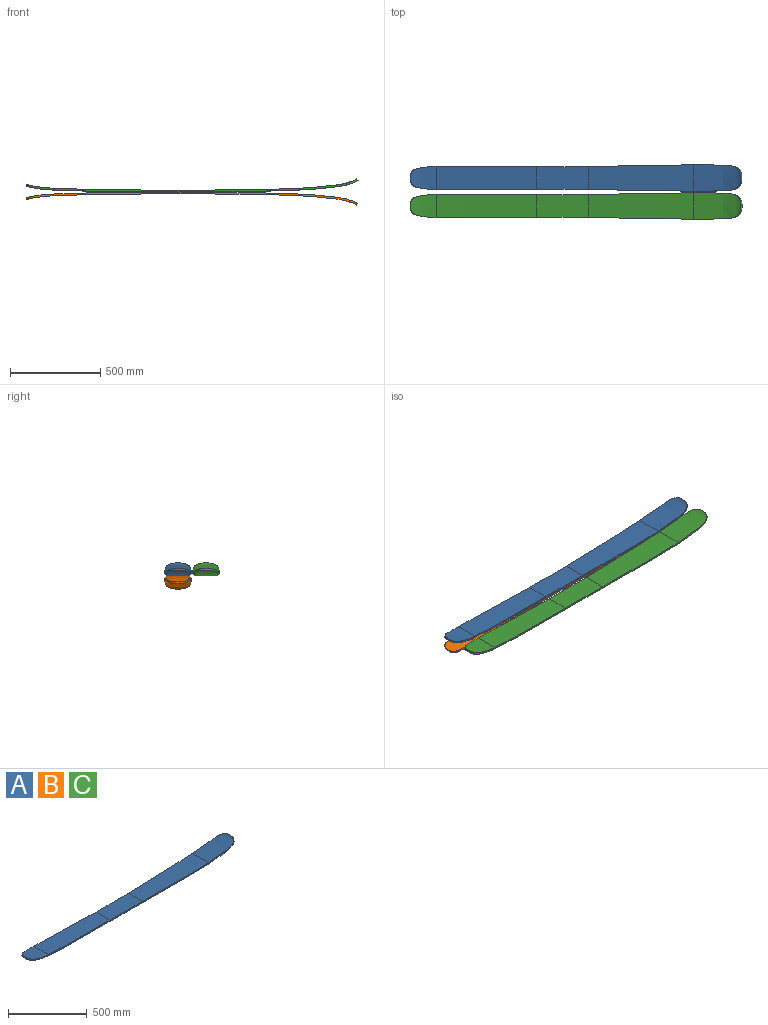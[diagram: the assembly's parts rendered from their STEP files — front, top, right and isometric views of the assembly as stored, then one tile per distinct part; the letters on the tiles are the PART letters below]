
ASSEMBLY  parts=3 mates=1
PART A: 34 faces, bbox 1840x146x72.7 mm
  f0: bspline ~43.73x36.32mm, area 603.5mm2, adj f1,f23,f24,f29
  f1: plane 15.1x9.66mm, normal (-0.97,0,0.26), area 151mm2, adj f0,f2,f24,f29
  f2: bspline ~43.73x36.32mm, area 603.5mm2, adj f1,f3,f24,f29
  f3: bspline ~91.78x21.48mm, area 922.4mm2, adj f2,f4,f24,f29
  f4: bspline ~18.68x10.97mm, area 181.8mm2, adj f3,f5,f24,f29
  f5: bspline ~150.89x15.46mm, area 1506.5mm2, adj f4,f6,f26,f31
  f6: bspline ~405.67x15.9mm, area 4056mm2, adj f5,f7,f26,f31
  f7: cylinder r=27015.71mm len=290mm, axis (0,0,1), area 2900mm2, adj f6,f8,f27,f32
  f8: bspline ~415.36x16.49mm, area 4153.2mm2, adj f7,f9,f28,f33
  f9: bspline ~168.68x16.93mm, area 1684.3mm2, adj f8,f10,f28,f33
  f10: bspline ~157.95x26.12mm, area 1577.8mm2, adj f9,f11,f25,f30
  f11: bspline ~65.82x24.18mm, area 656.3mm2, adj f10,f12,f25,f30
  f12: bspline ~54.85x47.65mm, area 784.1mm2, adj f11,f13,f25,f30
  f13: plane 19.91x7.66mm, normal (0.77,0,0.64), area 199.1mm2, adj f12,f14,f25,f30
  f14: bspline ~54.85x47.65mm, area 784.1mm2, adj f13,f15,f25,f30
  f15: bspline ~65.82x24.18mm, area 656.3mm2, adj f14,f16,f25,f30
  f16: bspline ~157.95x26.12mm, area 1577.8mm2, adj f15,f17,f25,f30
  f17: bspline ~168.68x16.93mm, area 1684.3mm2, adj f16,f18,f28,f33
  f18: bspline ~415.36x16.49mm, area 4153.2mm2, adj f17,f19,f28,f33
  f19: cylinder r=27015.71mm len=290mm, axis (0,0,1), area 2900mm2, adj f18,f20,f27,f32
  f20: bspline ~405.67x15.9mm, area 4056mm2, adj f19,f21,f26,f31
  f21: bspline ~150.89x15.46mm, area 1506.5mm2, adj f20,f22,f26,f31
  f22: bspline ~18.68x10.97mm, area 181.8mm2, adj f21,f23,f24,f29
  f23: bspline ~91.78x21.48mm, area 922.4mm2, adj f0,f22,f24,f29
  f24: extruded ~141.59x128.78mm, area 15750.3mm2, adj f0,f1,f2,f3,f4,f22,f23,f26
  f25: extruded ~260.37x146mm, area 36382mm2, adj f10,f11,f12,f13,f14,f15,f16,f28
  f26: extruded ~555.82x133mm, area 71616.6mm2, adj f5,f6,f20,f21,f24,f27
  f27: plane 290x127.36mm, normal (0,0,1), area 36449mm2, adj f7,f19,f26,f28
  f28: extruded ~583.2x145.97mm, area 79660.6mm2, adj f8,f9,f17,f18,f25,f27
  f29: extruded ~143.75x128.78mm, area 15983.7mm2, adj f0,f1,f2,f3,f4,f22,f23,f31
  f30: extruded ~266.29x146mm, area 37097.2mm2, adj f10,f11,f12,f13,f14,f15,f16,f33
  f31: extruded ~556.25x133mm, area 71672.1mm2, adj f5,f6,f20,f21,f29,f32
  f32: plane 290x127.36mm, normal (0,0,-1), area 36449mm2, adj f7,f19,f31,f33
  f33: extruded ~583.71x145.97mm, area 79730.4mm2, adj f8,f9,f17,f18,f30,f32
PART B: same geometry as A
PART C: same geometry as A
PLACE A t=(-565.32,-342.94,168.9)mm
PLACE B rot(axis=(1,0,0),180deg) t=(-565.32,-342.94,-11.1)mm
PLACE C t=(-564.96,-498.12,169.3)mm
MATE fastened B.f32 <-> A.f32  axis (0,0,1) through (-1309.87,-342.94,78.9)mm
